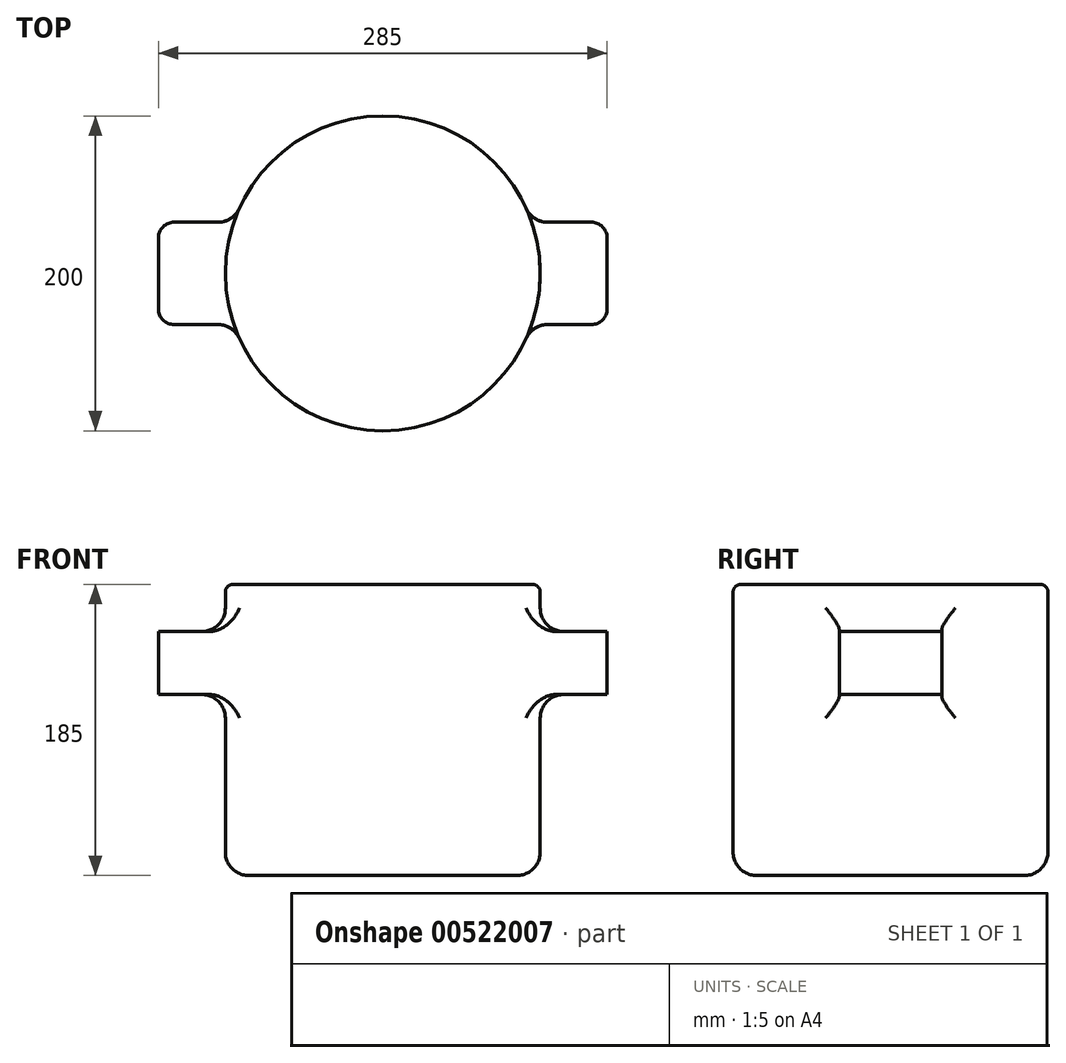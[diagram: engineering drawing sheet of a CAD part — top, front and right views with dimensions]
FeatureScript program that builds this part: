
annotation { "Feature Type Name" : "Feature", "Feature Type Description" : "" }
export const myFeature = defineFeature(function(context is Context, id is Id, definition is map)
    precondition{}
    {
        {
            var Q0;
            Q0=qCreatedBy(makeId("Top.planeOp"),FACE);
            var sketch = newSketch(context, id + "F0", { "sketchPlane" : qUnion([Q0])});
            skCircle(sketch, "E0", {"center": v(0, 0) * mm, "radius": 100 * mm});
            skSolve(sketch);
        }
        {
            var Q0;
            Q0=makeQuery(id+"F0.imprint","IMPRINT",FACE,{"disambiguationData":[TD([[makeQuery(id+"F0.imprint","IMPRINT",EDGE,{"derivedFrom":sQuery(id+"F0.wireOp",EDGE,"E0")}),1.0]])]});
            extrude(context, id + "F1", {"entities" : qUnion([Q0]), "depth" : 185 * mm, "offsetDistance" : 25 * mm});
        }
        {
            var Q0;
            Q0=qCreatedBy(makeId("Front.planeOp"),FACE);
            var sketch = newSketch(context, id + "F2", { "sketchPlane" : qUnion([Q0])});
            skLineSegment(sketch, "E1.bottom", {"start": v(-142.5, 155) * mm, "end": v(-80, 155) * mm});
            skLineSegment(sketch, "E1.top", {"start": v(-142.5, 115) * mm, "end": v(-80, 115) * mm});
            skLineSegment(sketch, "E1.left", {"start": v(-142.5, 155) * mm, "end": v(-142.5, 115) * mm});
            skLineSegment(sketch, "E1.right", {"start": v(-80, 155) * mm, "end": v(-80, 115) * mm});
            skLineSegment(sketch, "E2.bottom", {"start": v(80, 155) * mm, "end": v(142.5, 155) * mm});
            skLineSegment(sketch, "E2.top", {"start": v(80, 115) * mm, "end": v(142.5, 115) * mm});
            skLineSegment(sketch, "E2.left", {"start": v(80, 155) * mm, "end": v(80, 115) * mm});
            skLineSegment(sketch, "E2.right", {"start": v(142.5, 155) * mm, "end": v(142.5, 115) * mm});
            skLineSegment(sketch, "E3", {"start": v(-80, 115) * mm, "end": v(0, 115) * mm, "construction": true});
            skLineSegment(sketch, "E4", {"start": v(0, 115) * mm, "end": v(80, 115) * mm, "construction": true});
            skSolve(sketch);
        }
        {
            var Q0;
            Q0=makeQuery(id+"F2.imprint","IMPRINT",FACE,{"disambiguationData":[TD([[makeQuery(id+"F2.imprint","IMPRINT",EDGE,{"derivedFrom":sQuery(id+"F2.wireOp",EDGE,"E1.bottom")}),-1.0]])]});
            var Q1;
            Q1=makeQuery(id+"F2.imprint","IMPRINT",FACE,{"disambiguationData":[TD([[makeQuery(id+"F2.imprint","IMPRINT",EDGE,{"derivedFrom":sQuery(id+"F2.wireOp",EDGE,"E2.bottom")}),-1.0]])]});
            extrude(context, id + "F3", {"entities" : qUnion([Q0, Q1]), "operationType" : NewBodyOperationType.ADD, "depth" : (65 / 2) * mm, "offsetDistance" : 25 * mm, "hasSecondDirection" : true, "secondDirectionOppositeDirection" : true, "secondDirectionDepth" : (65 / 2) * mm});
        }
        {
            var Q0;
            Q0=makeQuery(id+"F3.opExtrude","CAP_EDGE",EDGE,{"disambiguationData":[OSD([sQuery(id+"F2.wireOp",EDGE,"E1.left")])],"isStart":false});
            var Q1;
            Q1=makeQuery(id+"F3.opExtrude","CAP_EDGE",EDGE,{"disambiguationData":[OSD([sQuery(id+"F2.wireOp",EDGE,"E1.left")])],"isStart":true});
            var Q2;
            Q2=makeQuery(id+"F3.opExtrude","CAP_EDGE",EDGE,{"disambiguationData":[OSD([sQuery(id+"F2.wireOp",EDGE,"E2.right")])],"isStart":false});
            var Q3;
            Q3=makeQuery(id+"F3.opExtrude","CAP_EDGE",EDGE,{"disambiguationData":[OSD([sQuery(id+"F2.wireOp",EDGE,"E2.right")])],"isStart":true});
            fillet(context, id + "F4", {"entities" : qUnion([Q0, Q1, Q2, Q3]), "radius" : 10 * mm, "tangentPropagation" : true, "allowEdgeOverflow" : false});
        }
        {
            var Q0;
            Q0=makeQuery(id+"F1.opExtrude","CAP_EDGE",EDGE,{"disambiguationData":[OSD([sQuery(id+"F0.wireOp",EDGE,"E0")])],"isStart":false});
            fillet(context, id + "F5", {"entities" : qUnion([Q0]), "radius" : 5 * mm, "tangentPropagation" : true, "allowEdgeOverflow" : false});
        }
        {
            var Q0;
            Q0=makeQuery(id+"F1.opExtrude","SWEPT_FACE",FACE,{"disambiguationData":[OSD([sQuery(id+"F0.wireOp",EDGE,"E0")])]});
            fillet(context, id + "F6", {"entities" : qUnion([Q0]), "radius" : 15 * mm, "tangentPropagation" : true, "allowEdgeOverflow" : false});
        }
    });
